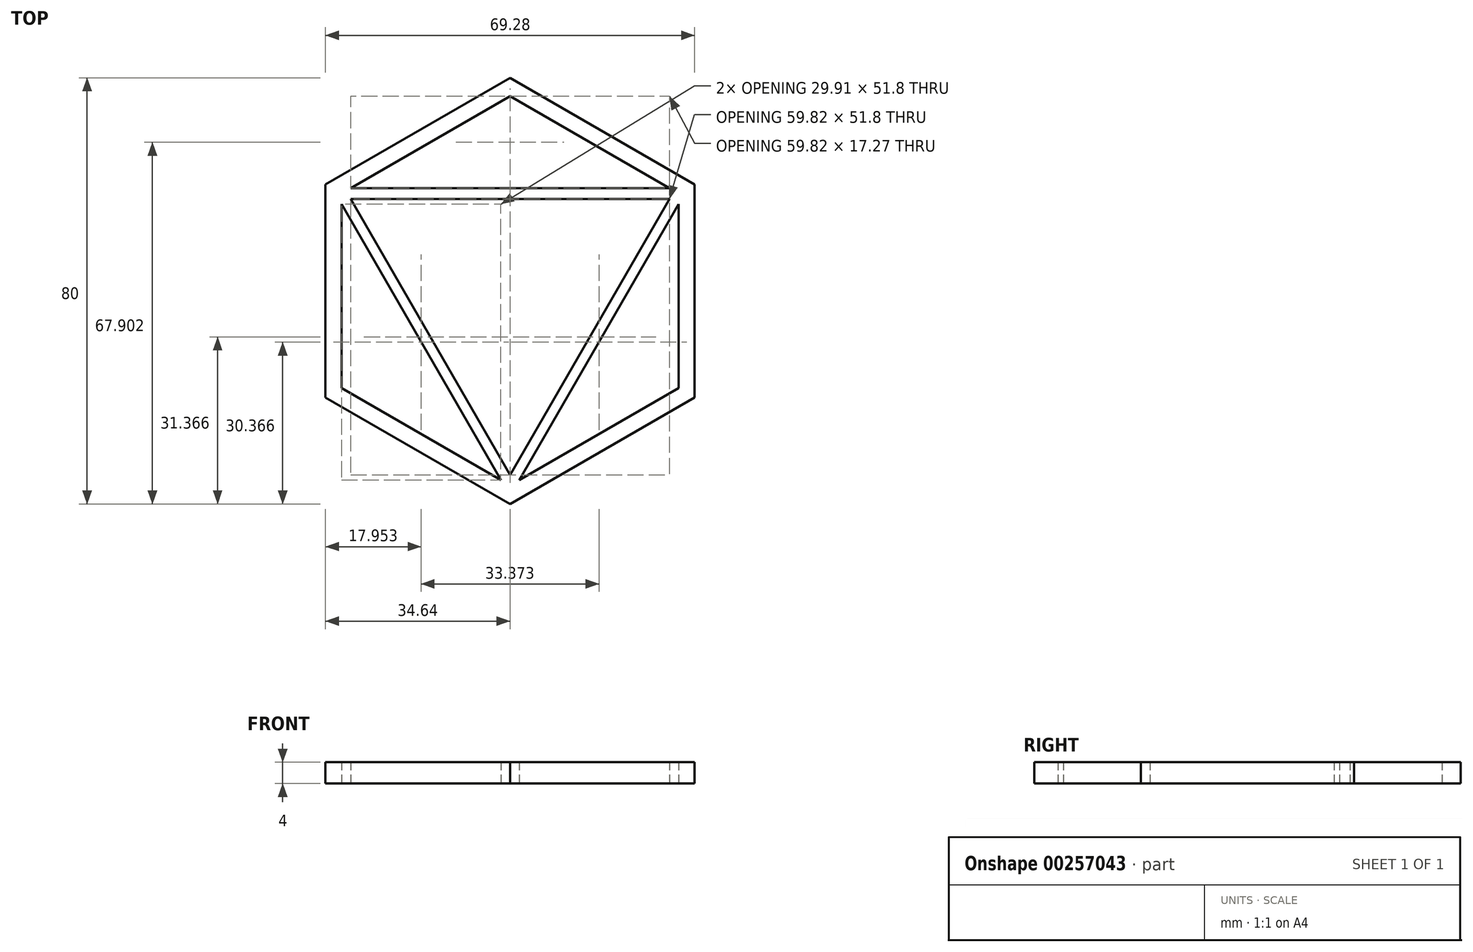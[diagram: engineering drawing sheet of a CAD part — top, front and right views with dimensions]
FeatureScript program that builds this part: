
annotation { "Feature Type Name" : "Feature", "Feature Type Description" : "" }
export const myFeature = defineFeature(function(context is Context, id is Id, definition is map)
    precondition{}
    {
        {
            var Q0;
            Q0=qCreatedBy(makeId("Top.planeOp"),FACE);
            var sketch = newSketch(context, id + "F0", { "sketchPlane" : qUnion([Q0])});
            skCircle(sketch, "E0.cCircle", {"center": v(0, 0) * mm, "radius": 34.64 * mm, "construction": true});
            skLineSegment(sketch, "E0.0", {"start": v(34.64, 20) * mm, "end": v(34.64, -20) * mm});
            skLineSegment(sketch, "E0.1", {"start": v(34.64, -20) * mm, "end": v(0, -40) * mm});
            skLineSegment(sketch, "E0.2", {"start": v(0, -40) * mm, "end": v(-34.64, -20) * mm});
            skLineSegment(sketch, "E0.3", {"start": v(-34.64, -20) * mm, "end": v(-34.64, 20) * mm});
            skLineSegment(sketch, "E0.4", {"start": v(-34.64, 20) * mm, "end": v(0, 40) * mm});
            skLineSegment(sketch, "E0.5", {"start": v(0, 40) * mm, "end": v(34.64, 20) * mm});
            skPoint(sketch, "E0.0.midPoint", {"position": v(34.64, 0) * mm});
            skSolve(sketch);
        }
        {
            var Q0;
            Q0=makeQuery(id+"F0.imprint","IMPRINT",FACE,{"disambiguationData":[TD([[makeQuery(id+"F0.imprint","IMPRINT",EDGE,{"derivedFrom":sQuery(id+"F0.wireOp",EDGE,"E0.0")}),-1.0]])]});
            extrude(context, id + "F1", {"entities" : qUnion([Q0]), "depth" : 4 * mm});
        }
        {
            var Q0;
            Q0=qCreatedBy(makeId("Top.planeOp"),FACE);
            var sketch = newSketch(context, id + "F2", { "sketchPlane" : qUnion([Q0])});
            skLineSegment(sketch, "E1.0", {"start": v(31.64, -18.27) * mm, "end": v(1.73, -35.54) * mm});
            skLineSegment(sketch, "E1.1", {"start": v(-31.64, -18.27) * mm, "end": v(-31.64, 16.27) * mm});
            skLineSegment(sketch, "E1.2", {"start": v(-29.9, 19.27) * mm, "end": v(0, 36.54) * mm});
            skLineSegment(sketch, "E1.3", {"start": v(-1.73, -35.54) * mm, "end": v(-31.64, -18.27) * mm});
            skLineSegment(sketch, "E1.4", {"start": v(0, 36.54) * mm, "end": v(29.9, 19.27) * mm});
            skLineSegment(sketch, "E1.5", {"start": v(31.64, 16.27) * mm, "end": v(31.64, -18.27) * mm});
            skLineSegment(sketch, "E2.0", {"start": v(0, -40) * mm, "end": v(-34.64, -20) * mm});
            skLineSegment(sketch, "E3.0", {"start": v(34.64, -20) * mm, "end": v(0, -40) * mm});
            skLineSegment(sketch, "E4.0", {"start": v(34.64, 20) * mm, "end": v(34.64, -20) * mm});
            skLineSegment(sketch, "E5.0", {"start": v(0, 40) * mm, "end": v(34.64, 20) * mm});
            skLineSegment(sketch, "E6.0", {"start": v(-34.64, 20) * mm, "end": v(0, 40) * mm});
            skLineSegment(sketch, "E7.0", {"start": v(-34.64, -20) * mm, "end": v(-34.64, 20) * mm});
            skLineSegment(sketch, "E8.0", {"start": v(-31.64, 16.27) * mm, "end": v(-1.73, -35.54) * mm});
            skLineSegment(sketch, "E8.1", {"start": v(29.9, 19.27) * mm, "end": v(-29.9, 19.27) * mm});
            skLineSegment(sketch, "E8.2", {"start": v(31.64, 16.27) * mm, "end": v(1.73, -35.54) * mm});
            skLineSegment(sketch, "E9.0", {"start": v(-29.9, 17.27) * mm, "end": v(0, -34.54) * mm});
            skLineSegment(sketch, "E9.1", {"start": v(29.9, 17.27) * mm, "end": v(-29.9, 17.27) * mm});
            skLineSegment(sketch, "E9.2", {"start": v(29.9, 17.27) * mm, "end": v(0, -34.54) * mm});
            skSolve(sketch);
        }
        {
            var Q0;
            Q0 = qSketchRegion(id + "F2", true);
            extrude(context, id + "F3", {"entities" : qUnion([Q0]), "operationType" : NewBodyOperationType.REMOVE, "endBound" : BoundingType.THROUGH_ALL, "depth" : 4 * mm});
        }
        {
            var Q0;
            Q0 = qSketchRegion(id + "F2", true);
            extrude(context, id + "F4", {"entities" : qUnion([Q0]), "depth" : 4 * mm});
        }
    });
